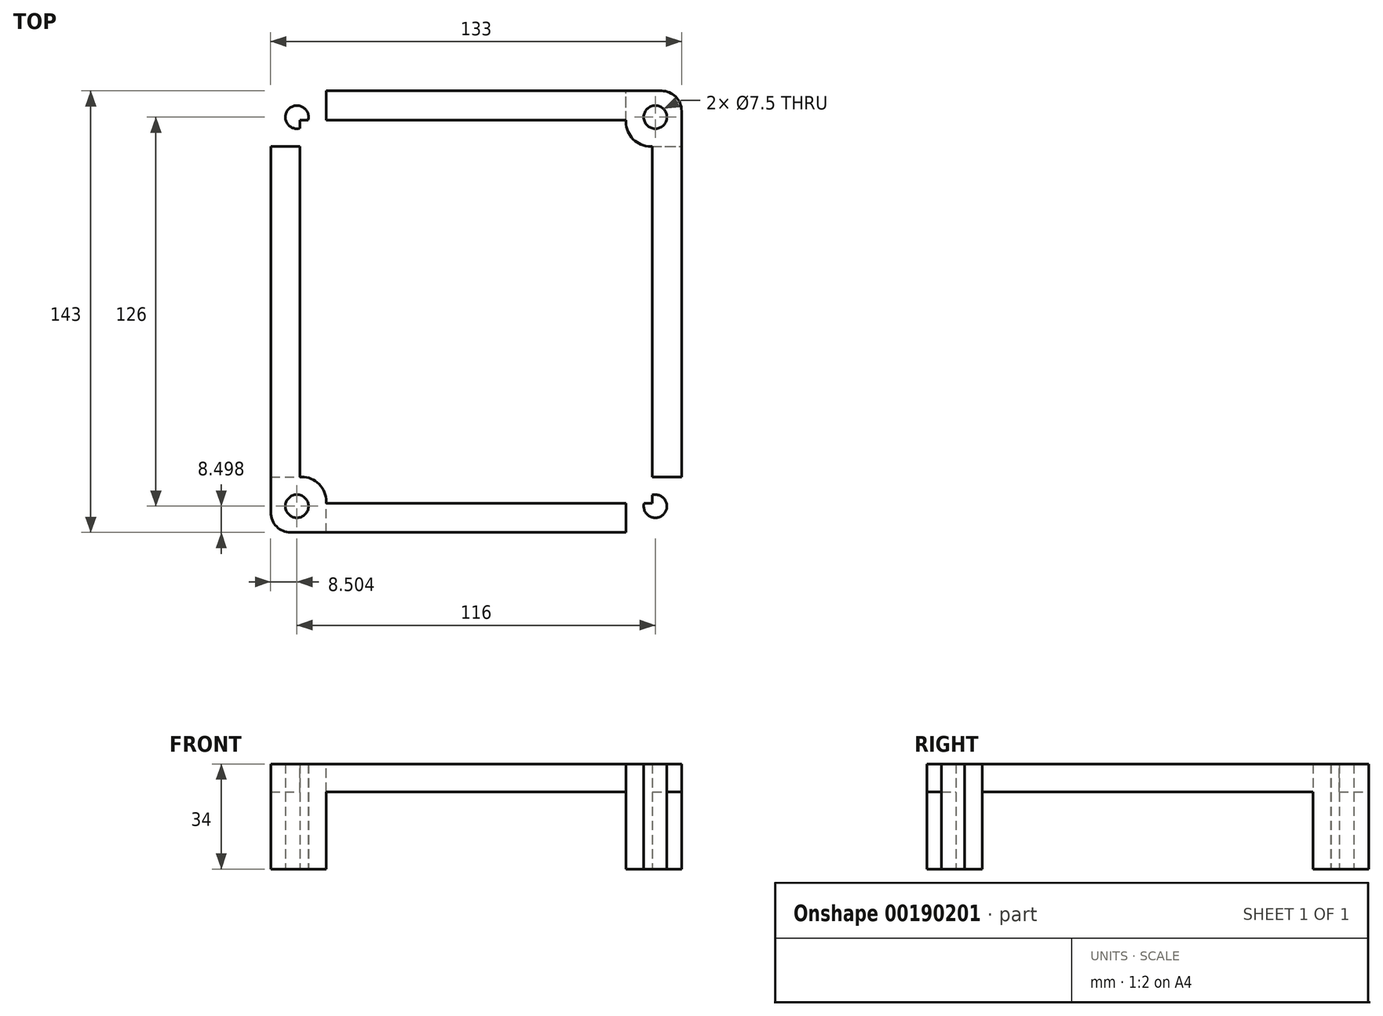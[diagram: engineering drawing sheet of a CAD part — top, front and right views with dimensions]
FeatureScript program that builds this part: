
annotation { "Feature Type Name" : "Feature", "Feature Type Description" : "" }
export const myFeature = defineFeature(function(context is Context, id is Id, definition is map)
    precondition{}
    {
        {
            var Q0;
            Q0=qCreatedBy(makeId("Top.planeOp"),FACE);
            var sketch = newSketch(context, id + "F0", { "sketchPlane" : qUnion([Q0])});
            skLineSegment(sketch, "E0.bottom", {"start": v(-58.87, -71.96) * mm, "end": v(61.13, -71.96) * mm});
            skLineSegment(sketch, "E0.top", {"start": v(-58.87, 71.04) * mm, "end": v(61.13, 71.04) * mm});
            skLineSegment(sketch, "E0.left", {"start": v(-65.37, -65.46) * mm, "end": v(-65.37, 64.54) * mm});
            skLineSegment(sketch, "E0.right", {"start": v(67.63, -65.46) * mm, "end": v(67.63, 64.54) * mm});
            skPoint(sketch, "E0.middle", {"position": v(1.13, -0.46) * mm});
            skPoint(sketch, "E1.visualSharp", {"position": v(67.63, 71.04) * mm});
            skArc(sketch, "E1.filletArc", {"start": v(67.63, 64.54) * mm, "mid": v(65.73, 69.13) * mm, "end": v(61.13, 71.04) * mm});
            skPoint(sketch, "E2.visualSharp", {"position": v(-65.37, 71.04) * mm});
            skArc(sketch, "E2.filletArc", {"start": v(-58.87, 71.04) * mm, "mid": v(-63.46, 69.13) * mm, "end": v(-65.37, 64.54) * mm});
            skPoint(sketch, "E3.visualSharp", {"position": v(67.63, -71.96) * mm});
            skArc(sketch, "E3.filletArc", {"start": v(61.13, -71.96) * mm, "mid": v(65.73, -70.06) * mm, "end": v(67.63, -65.46) * mm});
            skPoint(sketch, "E4.visualSharp", {"position": v(-65.37, -71.96) * mm});
            skArc(sketch, "E4.filletArc", {"start": v(-65.37, -65.46) * mm, "mid": v(-63.46, -70.06) * mm, "end": v(-58.87, -71.96) * mm});
            skLineSegment(sketch, "E5.bottom", {"start": v(-55.87, -62.46) * mm, "end": v(58.13, -62.46) * mm});
            skLineSegment(sketch, "E5.top", {"start": v(-55.87, 61.54) * mm, "end": v(58.13, 61.54) * mm});
            skLineSegment(sketch, "E5.left", {"start": v(-55.87, -62.46) * mm, "end": v(-55.87, 61.54) * mm});
            skLineSegment(sketch, "E5.right", {"start": v(58.13, -62.46) * mm, "end": v(58.13, 61.54) * mm});
            skSolve(sketch);
        }
        {
            var Q0;
            Q0 = qSketchRegion(id + "F0", true);
            extrude(context, id + "F1", {"entities" : qUnion([Q0]), "depth" : 34 * mm, "offsetDistance" : 25 * mm});
        }
        {
            var Q0;
            Q0=makeQuery(id+"F1.opExtrude","CAP_FACE",FACE,{"disambiguationData":[OSD([sQuery(id+"F0.wireOp",EDGE,"E0.bottom"),sQuery(id+"F0.wireOp",EDGE,"E0.top"),sQuery(id+"F0.wireOp",EDGE,"E0.left"),sQuery(id+"F0.wireOp",EDGE,"E0.right"),sQuery(id+"F0.wireOp",EDGE,"E1.filletArc"),sQuery(id+"F0.wireOp",EDGE,"E2.filletArc"),sQuery(id+"F0.wireOp",EDGE,"E3.filletArc"),sQuery(id+"F0.wireOp",EDGE,"E4.filletArc"),sQuery(id+"F0.wireOp",EDGE,"E5.bottom"),sQuery(id+"F0.wireOp",EDGE,"E5.top"),sQuery(id+"F0.wireOp",EDGE,"E5.left"),sQuery(id+"F0.wireOp",EDGE,"E5.right")])],"isStart":true});
            var sketch = newSketch(context, id + "F2", { "sketchPlane" : qUnion([Q0])});
            skLineSegment(sketch, "E6.bottom", {"start": v(-47.37, 96.67) * mm, "end": v(49.63, 96.67) * mm});
            skLineSegment(sketch, "E6.top", {"start": v(-47.37, -96.67) * mm, "end": v(49.63, -96.67) * mm});
            skLineSegment(sketch, "E6.left", {"start": v(-47.37, 96.67) * mm, "end": v(-47.37, -96.67) * mm});
            skLineSegment(sketch, "E6.right", {"start": v(49.63, 96.67) * mm, "end": v(49.63, -96.67) * mm});
            skPoint(sketch, "E6.middle", {"position": v(1.13, 0) * mm});
            skLineSegment(sketch, "E7.bottom", {"start": v(-90.86, 53.96) * mm, "end": v(135.08, 53.96) * mm});
            skLineSegment(sketch, "E7.top", {"start": v(-90.86, -53.04) * mm, "end": v(135.08, -53.04) * mm});
            skLineSegment(sketch, "E7.left", {"start": v(-90.86, 53.96) * mm, "end": v(-90.86, -53.04) * mm});
            skLineSegment(sketch, "E7.right", {"start": v(135.08, 53.96) * mm, "end": v(135.08, -53.04) * mm});
            skSolve(sketch);
        }
        {
            var Q0;
            Q0 = qSketchRegion(id + "F2", true);
            extrude(context, id + "F3", {"entities" : qUnion([Q0]), "operationType" : NewBodyOperationType.REMOVE, "oppositeDirection" : true, "depth" : 25 * mm, "offsetDistance" : 25 * mm});
        }
        {
            var Q0;
            Q0=qCreatedBy(makeId("Top.planeOp"),FACE);
            var sketch = newSketch(context, id + "F4", { "sketchPlane" : qUnion([Q0])});
            skLineSegment(sketch, "E8.bottom", {"start": v(-55.37, -53.96) * mm, "end": v(-65.37, -53.96) * mm});
            skLineSegment(sketch, "E8.top", {"start": v(-47.37, -71.96) * mm, "end": v(-58.87, -71.96) * mm});
            skLineSegment(sketch, "E8.left", {"start": v(-47.37, -61.96) * mm, "end": v(-47.37, -71.96) * mm});
            skLineSegment(sketch, "E8.right", {"start": v(-65.37, -53.96) * mm, "end": v(-65.37, -65.46) * mm});
            skPoint(sketch, "E9.visualSharp", {"position": v(-65.37, -71.96) * mm});
            skArc(sketch, "E9.filletArc", {"start": v(-65.37, -65.46) * mm, "mid": v(-63.46, -70.06) * mm, "end": v(-58.87, -71.96) * mm});
            skPoint(sketch, "E10.visualSharp", {"position": v(-47.37, -53.96) * mm});
            skArc(sketch, "E10.filletArc", {"start": v(-47.37, -61.96) * mm, "mid": v(-49.7, -56.3) * mm, "end": v(-55.37, -53.96) * mm});
            skCircle(sketch, "E11", {"center": v(-56.87, -63.46) * mm, "radius": 3.75 * mm});
            skLineSegment(sketch, "E12", {"start": v(1.13, -77.66) * mm, "end": v(1.13, 51.15) * mm});
            skLineSegment(sketch, "E13", {"start": v(-42.47, -0.46) * mm, "end": v(34.45, -0.46) * mm});
            skArc(sketch, "E14.MirrorCS", {"start": v(49.63, -61.96) * mm, "mid": v(51.98, -56.3) * mm, "end": v(57.63, -53.96) * mm});
            skPoint(sketch, "E15.MirrorP", {"position": v(67.63, -71.96) * mm});
            skArc(sketch, "E16.MirrorCS", {"start": v(67.63, -65.46) * mm, "mid": v(65.73, -70.06) * mm, "end": v(61.13, -71.96) * mm});
            skLineSegment(sketch, "E17.MirrorCS", {"start": v(67.63, -53.96) * mm, "end": v(67.63, -65.46) * mm});
            skCircle(sketch, "E18.MirrorC", {"center": v(59.13, -63.46) * mm, "radius": 3.75 * mm});
            skLineSegment(sketch, "E19.MirrorCS", {"start": v(49.63, -61.96) * mm, "end": v(49.63, -71.96) * mm});
            skLineSegment(sketch, "E20.MirrorCS", {"start": v(49.63, -71.96) * mm, "end": v(61.13, -71.96) * mm});
            skLineSegment(sketch, "E21.MirrorCS", {"start": v(57.63, -53.96) * mm, "end": v(67.63, -53.96) * mm});
            skPoint(sketch, "E22.MirrorP", {"position": v(49.63, -53.96) * mm});
            skLineSegment(sketch, "E23.MirrorCS", {"start": v(67.63, 53.04) * mm, "end": v(67.63, 64.54) * mm});
            skCircle(sketch, "E24.MirrorC", {"center": v(59.13, 62.54) * mm, "radius": 3.75 * mm});
            skLineSegment(sketch, "E25.MirrorCS", {"start": v(57.63, 53.04) * mm, "end": v(67.63, 53.04) * mm});
            skPoint(sketch, "E26.MirrorP", {"position": v(-65.37, 71.04) * mm});
            skArc(sketch, "E27.MirrorCS", {"start": v(67.63, 64.54) * mm, "mid": v(65.73, 69.13) * mm, "end": v(61.13, 71.04) * mm});
            skArc(sketch, "E28.MirrorCS", {"start": v(49.63, 61.04) * mm, "mid": v(51.98, 55.38) * mm, "end": v(57.63, 53.04) * mm});
            skPoint(sketch, "E29.MirrorP", {"position": v(49.63, 53.04) * mm});
            skLineSegment(sketch, "E30.MirrorCS", {"start": v(49.63, 71.04) * mm, "end": v(61.13, 71.04) * mm});
            skLineSegment(sketch, "E31.MirrorCS", {"start": v(-55.37, 53.04) * mm, "end": v(-65.37, 53.04) * mm});
            skLineSegment(sketch, "E32.MirrorCS", {"start": v(-47.37, 71.04) * mm, "end": v(-58.87, 71.04) * mm});
            skLineSegment(sketch, "E33.MirrorCS", {"start": v(-47.37, 61.04) * mm, "end": v(-47.37, 71.04) * mm});
            skPoint(sketch, "E34.MirrorP", {"position": v(-47.37, 53.04) * mm});
            skLineSegment(sketch, "E35.MirrorCS", {"start": v(-65.37, 53.04) * mm, "end": v(-65.37, 64.54) * mm});
            skLineSegment(sketch, "E36.MirrorCS", {"start": v(49.63, 61.04) * mm, "end": v(49.63, 71.04) * mm});
            skArc(sketch, "E37.MirrorCS", {"start": v(-65.37, 64.54) * mm, "mid": v(-63.46, 69.13) * mm, "end": v(-58.87, 71.04) * mm});
            skArc(sketch, "E38.MirrorCS", {"start": v(-47.37, 61.04) * mm, "mid": v(-49.7, 55.38) * mm, "end": v(-55.37, 53.04) * mm});
            skCircle(sketch, "E39.MirrorC", {"center": v(-56.87, 62.54) * mm, "radius": 3.75 * mm});
            skPoint(sketch, "E40.MirrorP", {"position": v(67.63, 71.04) * mm});
            skSolve(sketch);
        }
        {
            var Q0;
            Q0=makeQuery(id+"F4.imprint","IMPRINT",FACE,{"disambiguationData":[TD([[makeQuery(id+"F4.imprint","IMPRINT",EDGE,{"derivedFrom":sQuery(id+"F4.wireOp",EDGE,"E8.bottom")}),1.0]])]});
            var Q1;
            Q1=makeQuery(id+"F4.imprint","IMPRINT",FACE,{"disambiguationData":[TD([[makeQuery(id+"F4.imprint","IMPRINT",EDGE,{"derivedFrom":sQuery(id+"F4.wireOp",EDGE,"E14.MirrorCS")}),-1.0]])]});
            var Q2;
            Q2=makeQuery(id+"F4.imprint","IMPRINT",FACE,{"disambiguationData":[TD([[makeQuery(id+"F4.imprint","IMPRINT",EDGE,{"derivedFrom":sQuery(id+"F4.wireOp",EDGE,"E23.MirrorCS")}),1.0]])]});
            var Q3;
            Q3=makeQuery(id+"F4.imprint","IMPRINT",FACE,{"disambiguationData":[TD([[makeQuery(id+"F4.imprint","IMPRINT",EDGE,{"derivedFrom":sQuery(id+"F4.wireOp",EDGE,"E31.MirrorCS")}),-1.0]])]});
            extrude(context, id + "F5", {"entities" : qUnion([Q0, Q1, Q2, Q3]), "operationType" : NewBodyOperationType.ADD, "depth" : 34 * mm, "offsetDistance" : 25 * mm});
        }
        {
            var Q0;
            Q0=makeQuery(id+"F4.imprint","IMPRINT",FACE,{"disambiguationData":[TD([[makeQuery(id+"F4.imprint","IMPRINT",EDGE,{"derivedFrom":sQuery(id+"F4.wireOp",EDGE,"E11")}),1.0]])]});
            var Q1;
            Q1=makeQuery(id+"F4.imprint","IMPRINT",FACE,{"disambiguationData":[TD([[makeQuery(id+"F4.imprint","IMPRINT",EDGE,{"derivedFrom":sQuery(id+"F4.wireOp",EDGE,"E18.MirrorC")}),-1.0]])]});
            var Q2;
            Q2=makeQuery(id+"F4.imprint","IMPRINT",FACE,{"disambiguationData":[TD([[makeQuery(id+"F4.imprint","IMPRINT",EDGE,{"derivedFrom":sQuery(id+"F4.wireOp",EDGE,"E24.MirrorC")}),1.0]])]});
            var Q3;
            Q3=makeQuery(id+"F4.imprint","IMPRINT",FACE,{"disambiguationData":[TD([[makeQuery(id+"F4.imprint","IMPRINT",EDGE,{"derivedFrom":sQuery(id+"F4.wireOp",EDGE,"E39.MirrorC")}),-1.0]])]});
            extrude(context, id + "F6", {"entities" : qUnion([Q0, Q1, Q2, Q3]), "operationType" : NewBodyOperationType.REMOVE, "depth" : 34 * mm, "offsetDistance" : 25 * mm});
        }
    });
